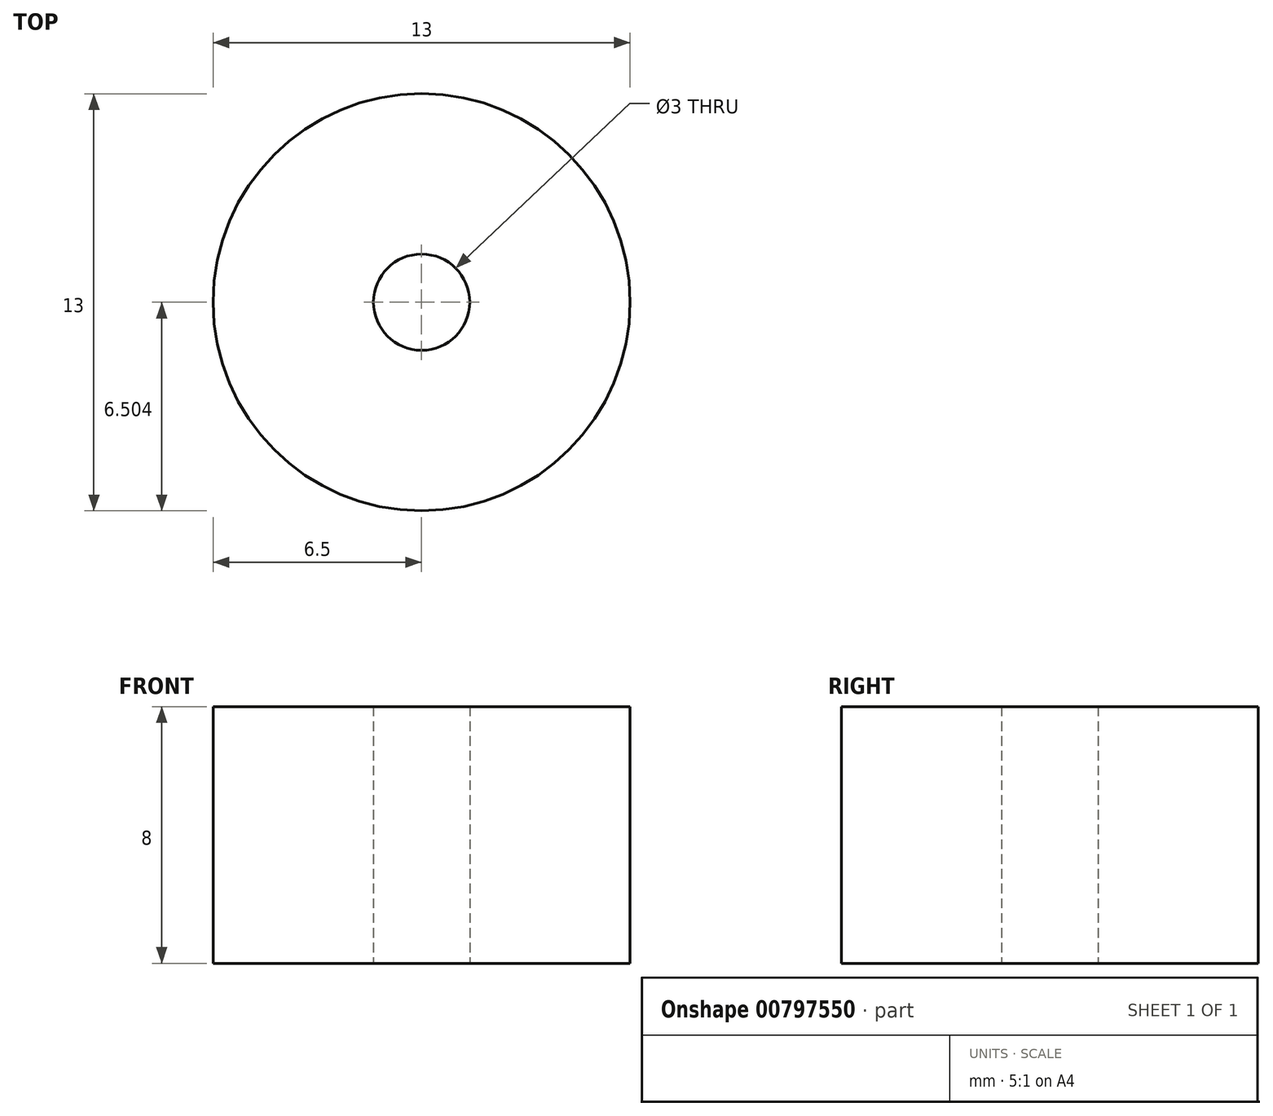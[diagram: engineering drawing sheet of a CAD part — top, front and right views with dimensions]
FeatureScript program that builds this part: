
annotation { "Feature Type Name" : "Feature", "Feature Type Description" : "" }
export const myFeature = defineFeature(function(context is Context, id is Id, definition is map)
    precondition{}
    {
        {
            var Q0;
            Q0=qCreatedBy(makeId("Top.planeOp"),FACE);
            var sketch = newSketch(context, id + "F0", { "sketchPlane" : qUnion([Q0])});
            skCircle(sketch, "E0", {"center": v(0, -1.69) * mm, "radius": 6.5 * mm});
            skCircle(sketch, "E1", {"center": v(0, -1.69) * mm, "radius": 1.5 * mm});
            skSolve(sketch);
        }
        {
            var Q0;
            Q0=makeQuery(id+"F0.imprint","IMPRINT",FACE,{"disambiguationData":[TD([[makeQuery(id+"F0.imprint","IMPRINT",EDGE,{"derivedFrom":sQuery(id+"F0.wireOp",EDGE,"E0")}),1.0]])]});
            extrude(context, id + "F1", {"entities" : qUnion([Q0]), "depth" : 8 * mm, "offsetDistance" : 25 * mm});
        }
    });
